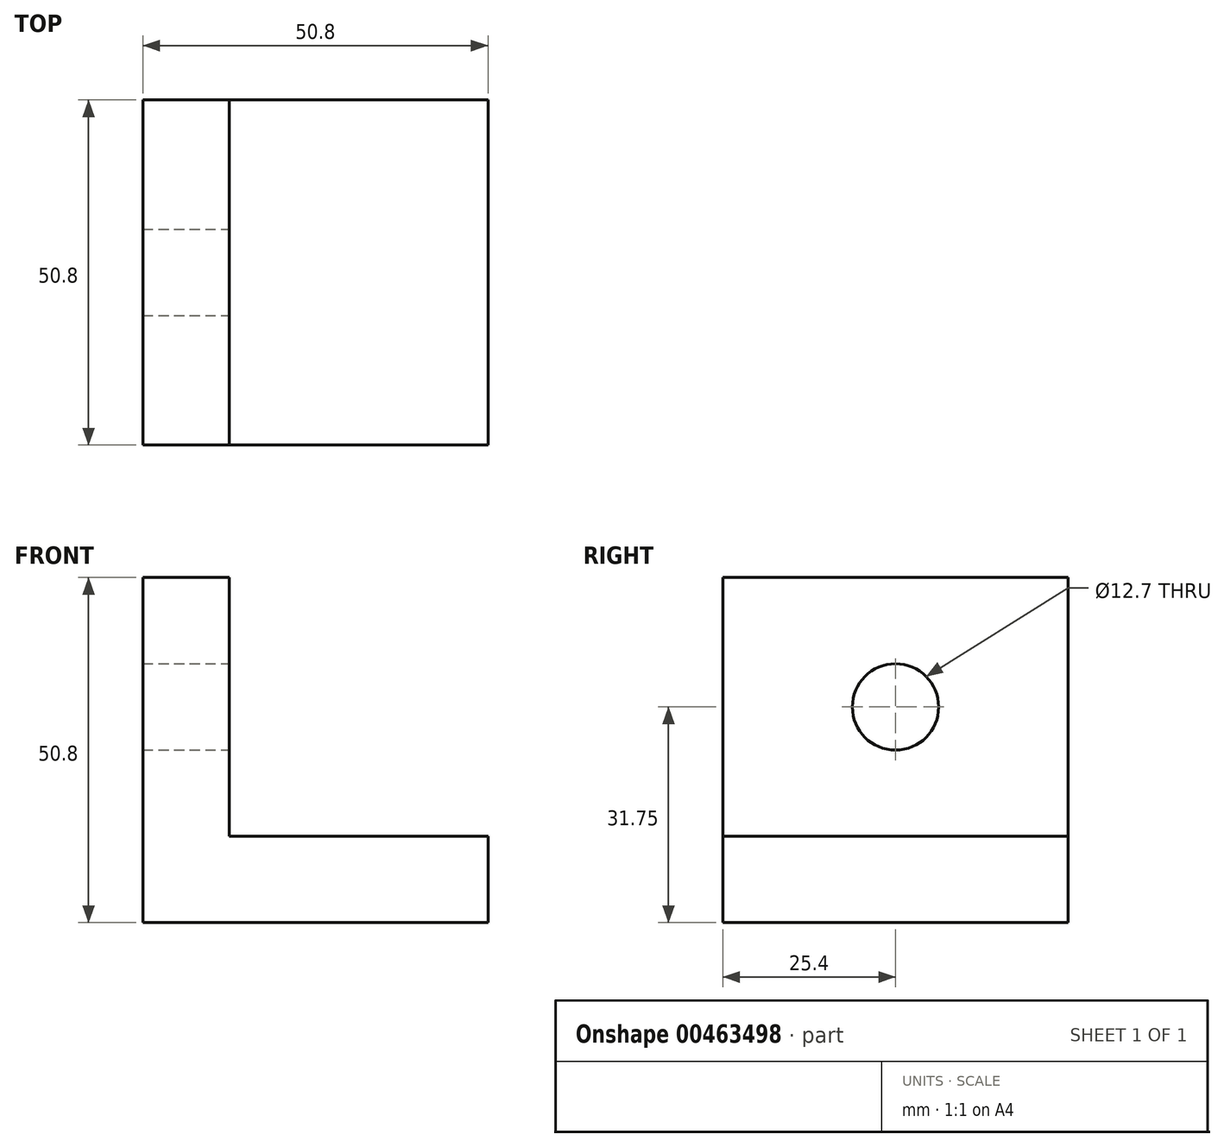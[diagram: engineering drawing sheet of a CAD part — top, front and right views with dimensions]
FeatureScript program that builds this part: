
annotation { "Feature Type Name" : "Feature", "Feature Type Description" : "" }
export const myFeature = defineFeature(function(context is Context, id is Id, definition is map)
    precondition{}
    {
        {
            var Q0;
            Q0=qCreatedBy(makeId("Top.planeOp"),FACE);
            var sketch = newSketch(context, id + "F0", { "sketchPlane" : qUnion([Q0])});
            skLineSegment(sketch, "E0.bottom", {"start": v(-22.18, 23.43) * mm, "end": v(28.62, 23.43) * mm});
            skLineSegment(sketch, "E0.top", {"start": v(-22.18, -27.37) * mm, "end": v(28.62, -27.37) * mm});
            skLineSegment(sketch, "E0.left", {"start": v(-22.18, 23.43) * mm, "end": v(-22.18, -27.37) * mm});
            skLineSegment(sketch, "E0.right", {"start": v(28.62, 23.43) * mm, "end": v(28.62, -27.37) * mm});
            skSolve(sketch);
        }
        {
            var Q0;
            Q0 = qSketchRegion(id + "F0", true);
            extrude(context, id + "F1", {"entities" : qUnion([Q0]), "depth" : 50.8 * mm});
        }
        {
            var Q0;
            Q0=makeQuery(id+"F1.opExtrude","SWEPT_FACE",FACE,{"disambiguationData":[OSD([sQuery(id+"F0.wireOp",EDGE,"E0.top")])]});
            var sketch = newSketch(context, id + "F2", { "sketchPlane" : qUnion([Q0])});
            skLineSegment(sketch, "E1.bottom", {"start": v(28.62, 50.8) * mm, "end": v(-9.48, 50.8) * mm});
            skLineSegment(sketch, "E1.top", {"start": v(28.62, 12.7) * mm, "end": v(-9.48, 12.7) * mm});
            skLineSegment(sketch, "E1.left", {"start": v(28.62, 50.8) * mm, "end": v(28.62, 12.7) * mm});
            skLineSegment(sketch, "E1.right", {"start": v(-9.48, 50.8) * mm, "end": v(-9.48, 12.7) * mm});
            skSolve(sketch);
        }
        {
            var Q0;
            Q0 = qSketchRegion(id + "F2", true);
            extrude(context, id + "F3", {"entities" : qUnion([Q0]), "operationType" : NewBodyOperationType.REMOVE, "oppositeDirection" : true, "depth" : 50.8 * mm});
        }
        {
            var Q0;
            Q0=makeQuery(id+"F3.boolean.opBoolean","COPY",FACE,{"derivedFrom":makeQuery(id+"F3.opExtrude","SWEPT_FACE",FACE,{"disambiguationData":[OSD([sQuery(id+"F2.wireOp",EDGE,"E1.right")])]})});
            var sketch = newSketch(context, id + "F4", { "sketchPlane" : qUnion([Q0])});
            skLineSegment(sketch, "E2", {"start": v(-27.37, 31.75) * mm, "end": v(23.43, 31.75) * mm, "construction": true});
            skLineSegment(sketch, "E3", {"start": v(-1.97, 12.7) * mm, "end": v(-1.97, 50.8) * mm, "construction": true});
            skCircle(sketch, "E4", {"center": v(-1.97, 31.75) * mm, "radius": 6.35 * mm});
            skSolve(sketch);
        }
        {
            var Q0;
            Q0 = qSketchRegion(id + "F4", true);
            extrude(context, id + "F5", {"entities" : qUnion([Q0]), "operationType" : NewBodyOperationType.REMOVE, "oppositeDirection" : true, "depth" : 25.4 * mm});
        }
    });
